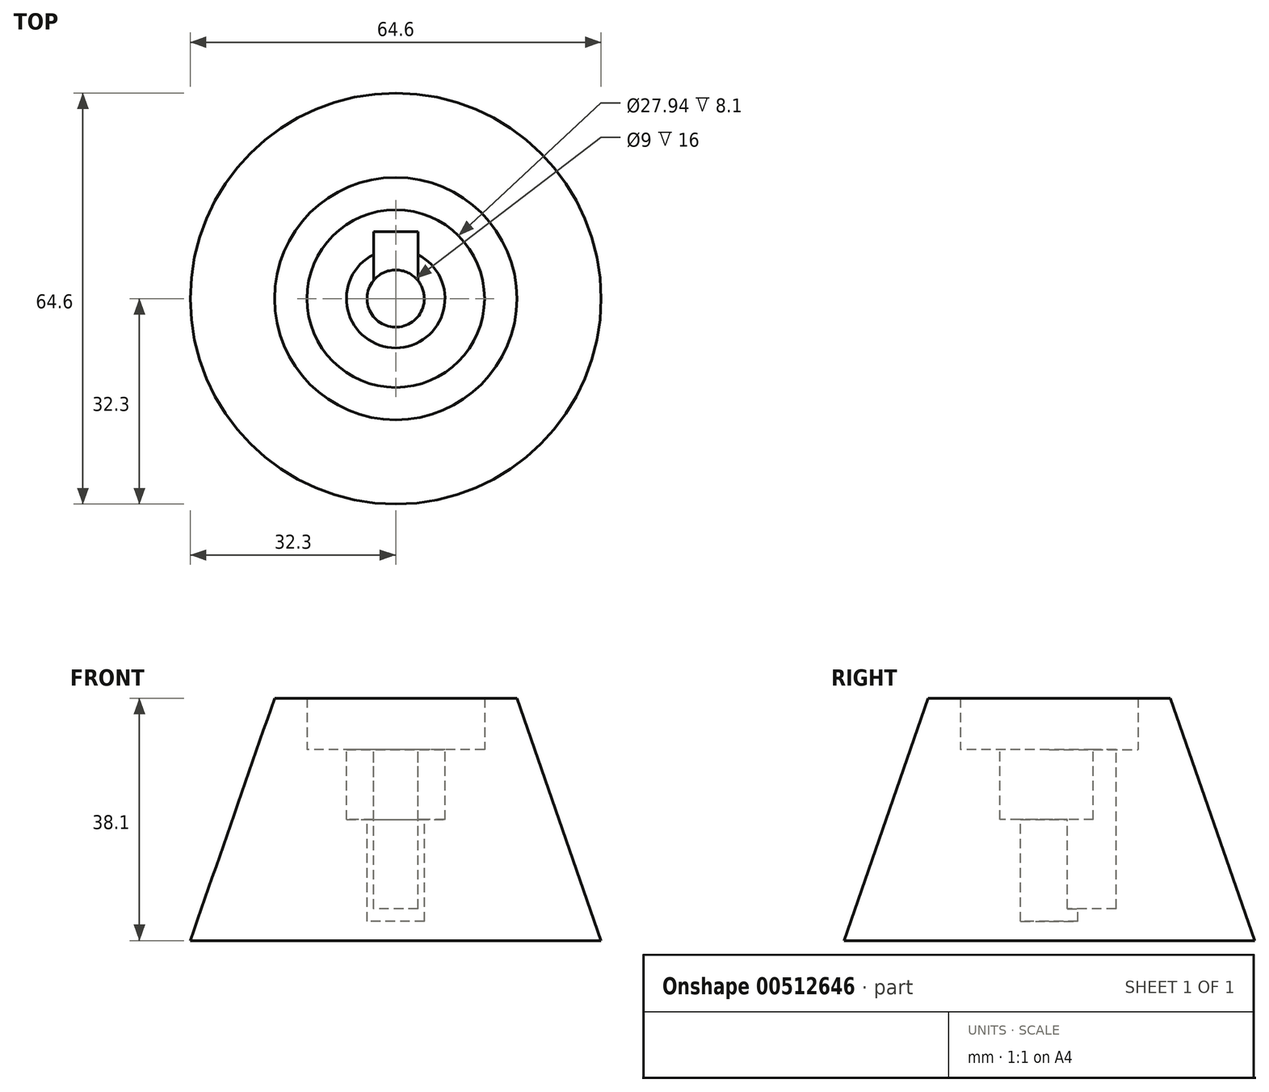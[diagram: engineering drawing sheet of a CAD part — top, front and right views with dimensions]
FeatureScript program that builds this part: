
annotation { "Feature Type Name" : "Feature", "Feature Type Description" : "" }
export const myFeature = defineFeature(function(context is Context, id is Id, definition is map)
    precondition{}
    {
        {
            var Q0;
            Q0=qCreatedBy(makeId("Front.planeOp"),FACE);
            var sketch = newSketch(context, id + "F0", { "sketchPlane" : qUnion([Q0])});
            skLineSegment(sketch, "E0", {"start": v(19.05, 38.1) * mm, "end": v(13.97, 38.1) * mm});
            skLineSegment(sketch, "E1", {"start": v(13.97, 38.1) * mm, "end": v(13.97, 0) * mm});
            skLineSegment(sketch, "E2", {"start": v(19.05, 38.1) * mm, "end": v(32.3, 0) * mm});
            skLineSegment(sketch, "E3", {"start": v(13.97, 0) * mm, "end": v(32.3, 0) * mm});
            skSolve(sketch);
        }
        {
            var Q0;
            Q0=qCreatedBy(makeId("Front.planeOp"),FACE);
            var sketch = newSketch(context, id + "F1", { "sketchPlane" : qUnion([Q0])});
            skLineSegment(sketch, "E4", {"start": v(0, 0) * mm, "end": v(0, 36.33) * mm});
            skSolve(sketch);
        }
        {
            var Q0;
            Q0=makeQuery(id+"F0.imprint","IMPRINT",FACE,{"disambiguationData":[TD([[makeQuery(id+"F0.imprint","IMPRINT",EDGE,{"derivedFrom":sQuery(id+"F0.wireOp",EDGE,"BsjQW3qa-pPV1-7GAX-QDmx-zntFj7AdCgJo")}),1.0]])]});
            var Q1;
            Q1=makeQuery(id+"F0.imprint","IMPRINT",FACE,{"disambiguationData":[TD([[makeQuery(id+"F0.imprint","IMPRINT",EDGE,{"derivedFrom":sQuery(id+"F0.wireOp",EDGE,"E0")}),1.0]])]});
            var Q2;
            Q2=sQuery(id+"F1.wireOp",EDGE,"E4");
            revolve(context, id + "F2", {"entities" : qUnion([Q0, Q1]), "axis" : qUnion([Q2]), "revolveType" : RevolveType.FULL});
        }
        {
            var Q0;
            Q0=qCreatedBy(makeId("Top.planeOp"),FACE);
            var sketch = newSketch(context, id + "F3", { "sketchPlane" : qUnion([Q0])});
            skCircle(sketch, "E5", {"center": v(0, 0) * mm, "radius": 14 * mm});
            skSolve(sketch);
        }
        {
            var Q0;
            Q0 = qSketchRegion(id + "F3", true);
            extrude(context, id + "F4", {"entities" : qUnion([Q0]), "operationType" : NewBodyOperationType.ADD, "depth" : 30 * mm, "offsetDistance" : 25 * mm});
        }
        {
            var Q0;
            Q0=makeQuery(id+"F4.opExtrude","CAP_FACE",FACE,{"disambiguationData":[OSD([sQuery(id+"F3.wireOp",EDGE,"E5")])],"isStart":false});
            var sketch = newSketch(context, id + "F5", { "sketchPlane" : qUnion([Q0])});
            skCircle(sketch, "E6", {"center": v(0, 0) * mm, "radius": 7.75 * mm});
            skSolve(sketch);
        }
        {
            var Q0;
            Q0=makeQuery(id+"F5.imprint","IMPRINT",FACE,{"disambiguationData":[TD([[makeQuery(id+"F5.imprint","IMPRINT",EDGE,{"derivedFrom":sQuery(id+"F5.wireOp",EDGE,"E6")}),-1.0]])]});
            var sketch = newSketch(context, id + "F6", { "sketchPlane" : qUnion([Q0])});
            skCircle(sketch, "E7", {"center": v(0, 0) * mm, "radius": 4.5 * mm});
            skSolve(sketch);
        }
        {
            var Q0;
            Q0 = qSketchRegion(id + "F6", true);
            extrude(context, id + "F7", {"entities" : qUnion([Q0]), "operationType" : NewBodyOperationType.REMOVE, "oppositeDirection" : true, "depth" : 27 * mm, "offsetDistance" : 25 * mm});
        }
        {
            var Q0;
            Q0 = qSketchRegion(id + "F5", true);
            extrude(context, id + "F8", {"entities" : qUnion([Q0]), "operationType" : NewBodyOperationType.REMOVE, "oppositeDirection" : true, "depth" : 11 * mm, "offsetDistance" : 25 * mm});
        }
        {
            var Q0;
            Q0=makeQuery(id+"F4.opExtrude","CAP_FACE",FACE,{"disambiguationData":[OSD([sQuery(id+"F3.wireOp",EDGE,"E5")])],"isStart":false});
            var sketch = newSketch(context, id + "F9", { "sketchPlane" : qUnion([Q0])});
            skLineSegment(sketch, "E8", {"start": v(0, 0) * mm, "end": v(3.5, 0) * mm});
            skLineSegment(sketch, "E9", {"start": v(3.5, 0) * mm, "end": v(3.5, 10.5) * mm});
            skLineSegment(sketch, "E10", {"start": v(3.5, 10.5) * mm, "end": v(-3.5, 10.5) * mm});
            skLineSegment(sketch, "E11", {"start": v(-3.5, 10.5) * mm, "end": v(-3.5, 0) * mm});
            skLineSegment(sketch, "E12", {"start": v(-3.5, 0) * mm, "end": v(0, 0) * mm});
            skSolve(sketch);
        }
        {
            var Q0;
            Q0 = qSketchRegion(id + "F9", true);
            extrude(context, id + "F10", {"entities" : qUnion([Q0]), "operationType" : NewBodyOperationType.REMOVE, "oppositeDirection" : true, "depth" : 25 * mm, "offsetDistance" : 25 * mm});
        }
    });
